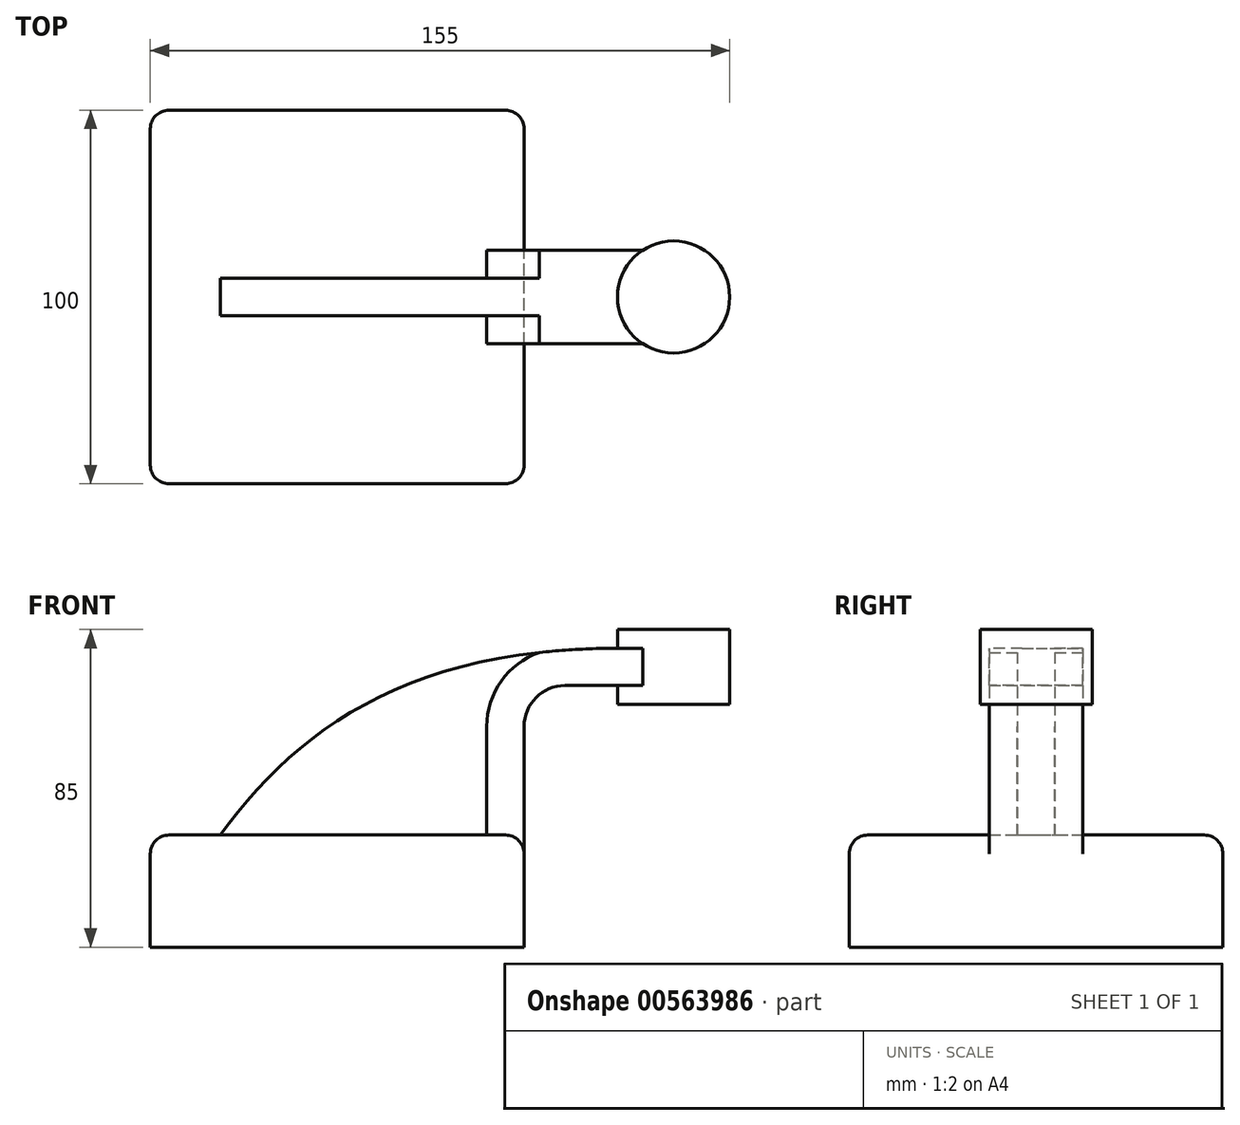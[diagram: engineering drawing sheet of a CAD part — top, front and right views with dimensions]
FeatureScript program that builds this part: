
annotation { "Feature Type Name" : "Feature", "Feature Type Description" : "" }
export const myFeature = defineFeature(function(context is Context, id is Id, definition is map)
    precondition{}
    {
        {
            var Q0;
            Q0=qCreatedBy(makeId("Front.planeOp"),FACE);
            var sketch = newSketch(context, id + "F0", { "sketchPlane" : qUnion([Q0])});
            skLineSegment(sketch, "E0.bottom", {"start": v(-50, 15) * mm, "end": v(50, 15) * mm});
            skLineSegment(sketch, "E0.top", {"start": v(-50, -15) * mm, "end": v(50, -15) * mm});
            skLineSegment(sketch, "E0.left", {"start": v(-50, 15) * mm, "end": v(-50, -15) * mm});
            skLineSegment(sketch, "E0.right", {"start": v(50, 15) * mm, "end": v(50, -15) * mm});
            skPoint(sketch, "E0.middle", {"position": v(0, 0) * mm});
            skLineSegment(sketch, "E1.bottom", {"start": v(105, 50) * mm, "end": v(75, 50) * mm});
            skLineSegment(sketch, "E1.top", {"start": v(105, 70) * mm, "end": v(75, 70) * mm});
            skLineSegment(sketch, "E1.left", {"start": v(105, 50) * mm, "end": v(105, 70) * mm});
            skLineSegment(sketch, "E1.right", {"start": v(75, 50) * mm, "end": v(75, 70) * mm});
            skPoint(sketch, "E1.middle", {"position": v(90, 60) * mm});
            skLineSegment(sketch, "E2", {"start": v(50, 15) * mm, "end": v(50, 44.06) * mm});
            skArc(sketch, "E3", {"start": v(50, 44.06) * mm, "mid": v(53.2, 51.8) * mm, "end": v(60.94, 55) * mm});
            skLineSegment(sketch, "E4", {"start": v(60.94, 55) * mm, "end": v(90, 55) * mm});
            skLineSegment(sketch, "E5.0", {"start": v(60.94, 65) * mm, "end": v(90, 65) * mm});
            skArc(sketch, "E5.1", {"start": v(40, 44.06) * mm, "mid": v(46.13, 58.87) * mm, "end": v(60.94, 65) * mm});
            skLineSegment(sketch, "E5.2", {"start": v(40, 15) * mm, "end": v(40, 44.06) * mm});
            skLineSegment(sketch, "E6", {"start": v(90, 70) * mm, "end": v(90, 50) * mm});
            skFitSpline(sketch, "E7", {"points": [v(75.47, 65) * mm, v(-31.31, 15) * mm], "startDerivative": vector(-170.7, 0) * mm, "endDerivative": vector(-60.78, -83.69) * mm});
            skSolve(sketch);
        }
        {
            var Q0;
            Q0=makeQuery(id+"F0.imprint","IMPRINT",FACE,{"disambiguationData":[TD([[makeQuery(id+"F0.imprint","IMPRINT",EDGE,{"derivedFrom":sQuery(id+"F0.wireOp",EDGE,"E0.top")}),1.0]])]});
            extrude(context, id + "F1", {"entities" : qUnion([Q0]), "endBound" : BoundingType.SYMMETRIC, "depth" : 100 * mm, "offsetDistance" : 25 * mm});
        }
        {
            var Q0;
            {var subQ1=sQuery(id+"F0.wireOp",EDGE,"E2");Q0=makeQuery(id+"F0.imprint","IMPRINT",FACE,{"disambiguationData":[TD([[makeQuery(id+"F0.imprint","IMPRINT",EDGE,{"derivedFrom":subQ1}),1.0]])]});}
            var Q1;
            {var subQ1=sQuery(id+"F0.wireOp",EDGE,"E4");var subQ7=sQuery(id+"F0.wireOp",EDGE,"E1.right");var subQ8=makeQuery(id+"F0.imprint","INTERSECT",VERTEX,{"derivedFrom":[subQ7,subQ1]});Q1=makeQuery(id+"F0.imprint","IMPRINT",FACE,{"disambiguationData":[TD([[makeQuery(id+"F0.imprint","IMPRINT",EDGE,{"disambiguationData":[TD([[subQ8,-1.0]])],"derivedFrom":subQ7}),-1.0]])]});}
            extrude(context, id + "F2", {"entities" : qUnion([Q0, Q1]), "operationType" : NewBodyOperationType.ADD, "endBound" : BoundingType.SYMMETRIC, "depth" : 25 * mm, "offsetDistance" : 25 * mm});
        }
        {
            var Q0;
            {var subQ0=sQuery(id+"F0.wireOp",EDGE,"E5.2");Q0=makeQuery(id+"F0.imprint","IMPRINT",FACE,{"disambiguationData":[TD([[makeQuery(id+"F0.imprint","IMPRINT",EDGE,{"derivedFrom":subQ0}),1.0]])]});}
            extrude(context, id + "F3", {"entities" : qUnion([Q0]), "operationType" : NewBodyOperationType.ADD, "endBound" : BoundingType.SYMMETRIC, "depth" : 10 * mm, "offsetDistance" : 25 * mm});
        }
        {
            var Q0;
            {var subQ4=sQuery(id+"F0.wireOp",EDGE,"E1.left");Q0=makeQuery(id+"F0.imprint","IMPRINT",FACE,{"disambiguationData":[TD([[makeQuery(id+"F0.imprint","IMPRINT",EDGE,{"derivedFrom":subQ4}),1.0]])]});}
            var Q1;
            Q1=sQuery(id+"F0.wireOp",EDGE,"E6");
            revolve(context, id + "F4", {"operationType" : NewBodyOperationType.ADD, "entities" : qUnion([Q0]), "axis" : qUnion([Q1]), "revolveType" : RevolveType.FULL});
        }
        {
            var Q0;
            Q0=makeQuery(id+"F1.opExtrude","CAP_EDGE",EDGE,{"disambiguationData":[OSD([sQuery(id+"F0.wireOp",EDGE,"E0.right")])],"isStart":false});
            var Q1;
            Q1=makeQuery(id+"F1.opExtrude","CAP_EDGE",EDGE,{"disambiguationData":[OSD([sQuery(id+"F0.wireOp",EDGE,"E0.left")])],"isStart":false});
            var Q2;
            Q2=makeQuery(id+"F1.opExtrude","CAP_EDGE",EDGE,{"disambiguationData":[OSD([sQuery(id+"F0.wireOp",EDGE,"E0.right")])],"isStart":true});
            var Q3;
            Q3=makeQuery(id+"F1.opExtrude","CAP_EDGE",EDGE,{"disambiguationData":[OSD([sQuery(id+"F0.wireOp",EDGE,"E0.left")])],"isStart":true});
            var Q4;
            Q4=makeQuery(id+"F1.opExtrude","CAP_EDGE",EDGE,{"disambiguationData":[OSD([sQuery(id+"F0.wireOp",EDGE,"E0.bottom")])],"isStart":true});
            var Q5;
            Q5=makeQuery(id+"F1.opExtrude","SWEPT_EDGE",EDGE,{"disambiguationData":[OSD([sQuery(id+"F0.wireOp",EDGE,"E0.bottom"),sQuery(id+"F0.wireOp",EDGE,"E0.left")])]});
            var Q6;
            Q6=makeQuery(id+"F1.opExtrude","CAP_EDGE",EDGE,{"disambiguationData":[OSD([sQuery(id+"F0.wireOp",EDGE,"E0.bottom")])],"isStart":false});
            var Q7;
            {var subQ0=sQuery(id+"F0.wireOp",EDGE,"E2");var subQ1=sQuery(id+"F0.wireOp",EDGE,"E0.bottom");var subQ2=sQuery(id+"F0.wireOp",EDGE,"E0.right");Q7=makeQuery(id+"F2.boolean.opBoolean","SPLIT",EDGE,{"disambiguationData":[TD([makeQuery(id+"F1.opExtrude","CAP_FACE",FACE,{"disambiguationData":[OSD([subQ1,sQuery(id+"F0.wireOp",EDGE,"E0.top"),sQuery(id+"F0.wireOp",EDGE,"E0.left"),subQ2])],"isStart":false})])],"derivedFrom":makeQuery(id+"F1.opExtrude","SWEPT_EDGE",EDGE,{"disambiguationData":[OSD([subQ1,subQ2,subQ0])]})});}
            var Q8;
            {var subQ0=sQuery(id+"F0.wireOp",EDGE,"E2");var subQ1=sQuery(id+"F0.wireOp",EDGE,"E0.bottom");var subQ2=sQuery(id+"F0.wireOp",EDGE,"E0.right");Q8=makeQuery(id+"F2.boolean.opBoolean","SPLIT",EDGE,{"disambiguationData":[TD([makeQuery(id+"F1.opExtrude","CAP_FACE",FACE,{"disambiguationData":[OSD([subQ1,sQuery(id+"F0.wireOp",EDGE,"E0.top"),sQuery(id+"F0.wireOp",EDGE,"E0.left"),subQ2])],"isStart":true})])],"derivedFrom":makeQuery(id+"F1.opExtrude","SWEPT_EDGE",EDGE,{"disambiguationData":[OSD([subQ1,subQ2,subQ0])]})});}
            fillet(context, id + "F5", {"entities" : qUnion([Q0, Q1, Q2, Q3, Q4, Q5, Q6, Q7, Q8]), "radius" : 5 * mm, "tangentPropagation" : true, "allowEdgeOverflow" : false});
        }
    });
